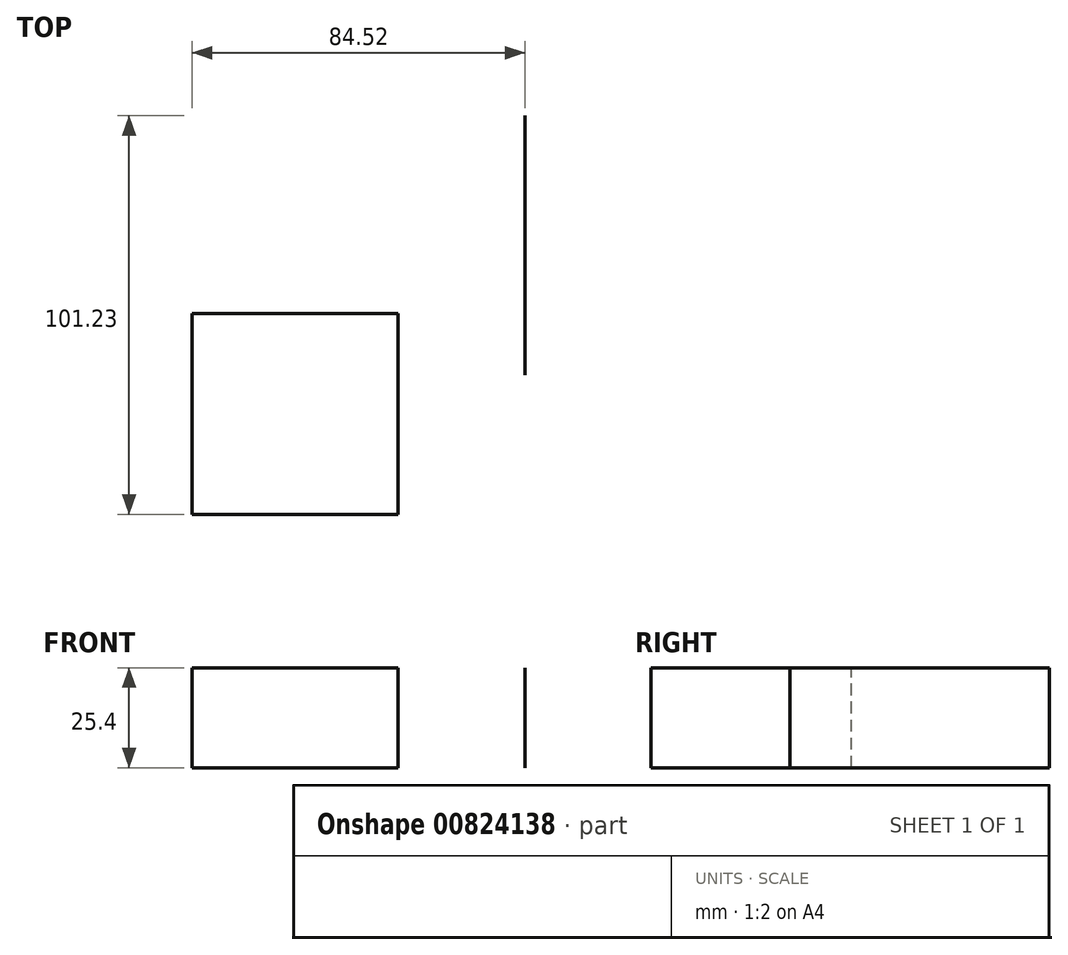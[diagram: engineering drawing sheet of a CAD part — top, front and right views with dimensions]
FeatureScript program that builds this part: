
annotation { "Feature Type Name" : "Feature", "Feature Type Description" : "" }
export const myFeature = defineFeature(function(context is Context, id is Id, definition is map)
    precondition{}
    {
        {
            var Q0;
            Q0=qCreatedBy(makeId("Top.planeOp"),FACE);
            var sketch = newSketch(context, id + "F0", { "sketchPlane" : qUnion([Q0])});
            skLineSegment(sketch, "E0.bottom", {"start": v(52.25, 50.96) * mm, "end": v(0, 50.96) * mm});
            skLineSegment(sketch, "E0.top", {"start": v(52.25, 0) * mm, "end": v(0, 0) * mm});
            skLineSegment(sketch, "E0.left", {"start": v(52.25, 50.96) * mm, "end": v(52.25, 0) * mm});
            skLineSegment(sketch, "E0.right", {"start": v(0, 50.96) * mm, "end": v(0, 0) * mm});
            skSolve(sketch);
        }
        {
            var Q0;
            Q0=makeQuery(id+"F0.imprint","IMPRINT",FACE,{"disambiguationData":[TD([[makeQuery(id+"F0.imprint","IMPRINT",EDGE,{"derivedFrom":sQuery(id+"F0.wireOp",EDGE,"E0.bottom")}),1.0]])]});
            var sketch = newSketch(context, id + "F1", { "sketchPlane" : qUnion([Q0])});
            skLineSegment(sketch, "E1.bottom", {"start": v(75.13, 101.23) * mm, "end": v(84.52, 101.23) * mm});
            skLineSegment(sketch, "E1.top", {"start": v(75.13, 35.35) * mm, "end": v(84.52, 35.35) * mm});
            skLineSegment(sketch, "E1.left", {"start": v(75.13, 101.23) * mm, "end": v(75.13, 35.35) * mm});
            skLineSegment(sketch, "E1.right", {"start": v(84.52, 101.23) * mm, "end": v(84.52, 35.35) * mm});
            skSolve(sketch);
        }
        {
            var Q0;
            Q0=sQuery(id+"F1.wireOp",EDGE,"E1.right");
            var Q1;
            Q1 = qBodyType(qCreatedBy(id + "F0" ,EDGE), BodyType.WIRE);
            extrude(context, id + "F2", {"bodyType" : ToolBodyType.SURFACE, "surfaceEntities" : qUnion([Q0, Q1]), "depth" : 25.4 * mm, "offsetDistance" : 25.4 * mm});
        }
    });
